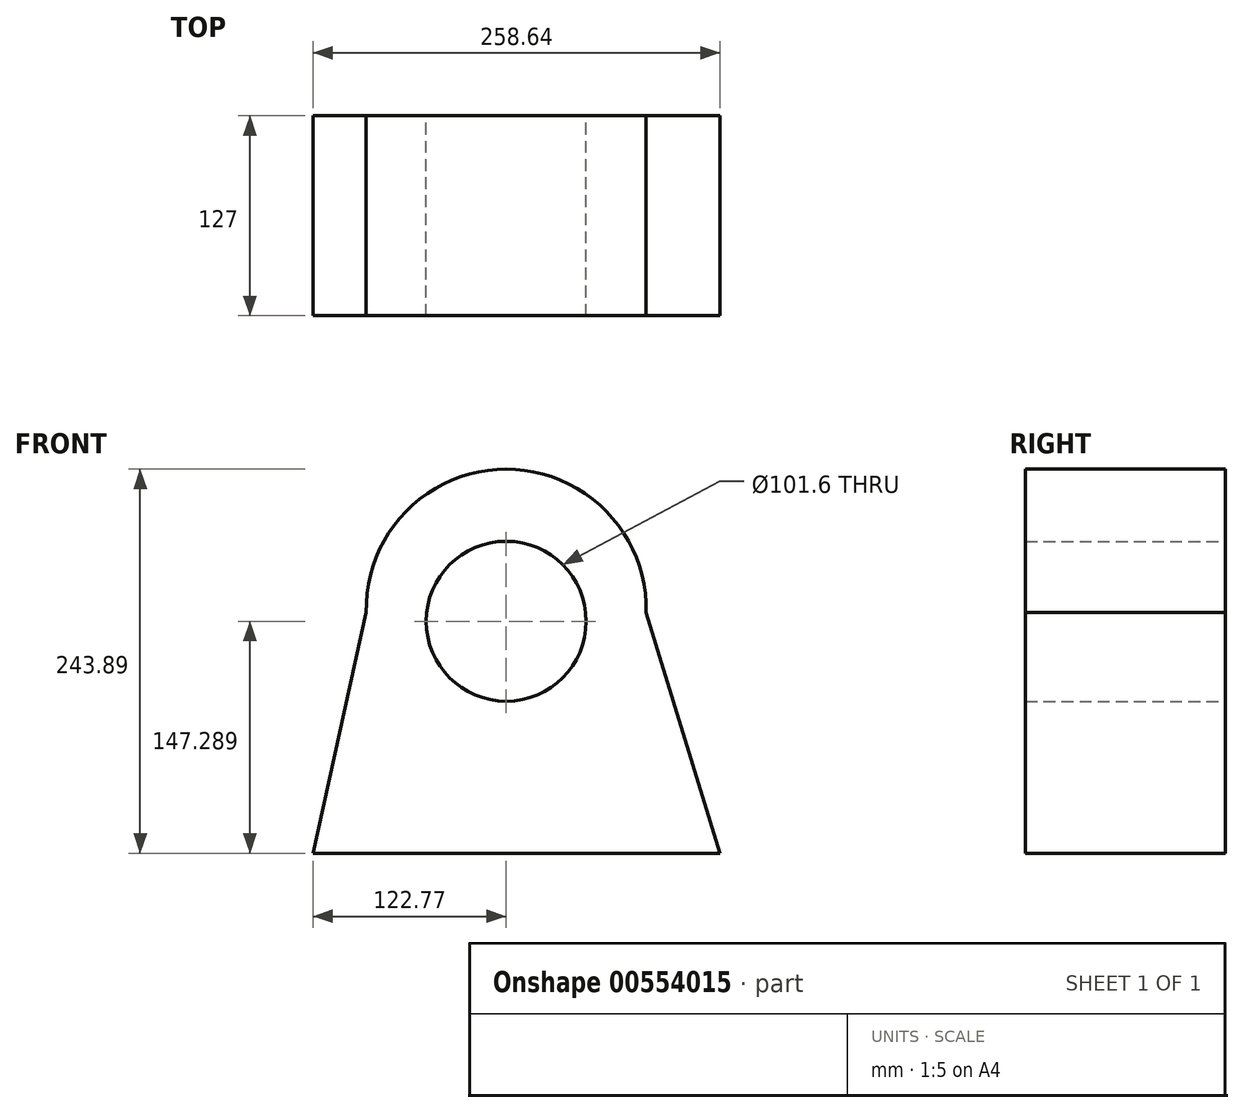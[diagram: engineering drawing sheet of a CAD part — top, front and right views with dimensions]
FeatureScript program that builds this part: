
annotation { "Feature Type Name" : "Feature", "Feature Type Description" : "" }
export const myFeature = defineFeature(function(context is Context, id is Id, definition is map)
    precondition{}
    {
        {
            var Q0;
            Q0=qCreatedBy(makeId("Front.planeOp"),FACE);
            var sketch = newSketch(context, id + "F0", { "sketchPlane" : qUnion([Q0])});
            skCircle(sketch, "E0", {"center": v(0, 49.35) * mm, "radius": 50.8 * mm});
            skCircle(sketch, "E1", {"center": v(0, 57.05) * mm, "radius": 88.9 * mm});
            skLineSegment(sketch, "E2", {"start": v(-155.97, 55.08) * mm, "end": v(-155.97, -33.82) * mm});
            skLineSegment(sketch, "E3", {"start": v(-155.97, -54.66) * mm, "end": v(-155.97, -118.16) * mm});
            skLineSegment(sketch, "E4", {"start": v(-122.77, -97.94) * mm, "end": v(-84.67, -97.94) * mm});
            skLineSegment(sketch, "E5", {"start": v(-77.23, -97.94) * mm, "end": v(49.77, -97.94) * mm});
            skLineSegment(sketch, "E6", {"start": v(63.46, -97.94) * mm, "end": v(126.96, -97.94) * mm});
            skLineSegment(sketch, "E7", {"start": v(-88.88, 55.08) * mm, "end": v(-122.77, -97.94) * mm});
            skLineSegment(sketch, "E8", {"start": v(88.88, 55.08) * mm, "end": v(135.87, -97.94) * mm});
            skLineSegment(sketch, "E9", {"start": v(135.87, -97.94) * mm, "end": v(117.77, -97.94) * mm});
            skLineSegment(sketch, "E10", {"start": v(49.77, -97.94) * mm, "end": v(63.46, -97.94) * mm});
            skLineSegment(sketch, "E11", {"start": v(-84.67, -97.94) * mm, "end": v(-77.23, -97.94) * mm});
            skLineSegment(sketch, "E12", {"start": v(-75.33, -43.29) * mm, "end": v(76.49, -43.29) * mm});
            skLineSegment(sketch, "E13", {"start": v(-75.33, -43.29) * mm, "end": v(-65.72, -65.55) * mm});
            skLineSegment(sketch, "E14", {"start": v(76.49, -43.29) * mm, "end": v(67.88, -67.58) * mm});
            skSolve(sketch);
        }
        {
            var Q0;
            Q0=makeQuery(id+"F0.imprint","IMPRINT",FACE,{"disambiguationData":[TD([[makeQuery(id+"F0.imprint","IMPRINT",EDGE,{"derivedFrom":sQuery(id+"F0.wireOp",EDGE,"E0")}),-1.0]])]});
            var Q1;
            Q1=makeQuery(id+"F0.imprint","IMPRINT",FACE,{"disambiguationData":[TD([[makeQuery(id+"F0.imprint","IMPRINT",EDGE,{"derivedFrom":sQuery(id+"F0.wireOp",EDGE,"E4")}),1.0]])]});
            extrude(context, id + "F1", {"entities" : qUnion([Q0, Q1]), "depth" : 127 * mm, "offsetDistance" : 25.4 * mm});
        }
    });
